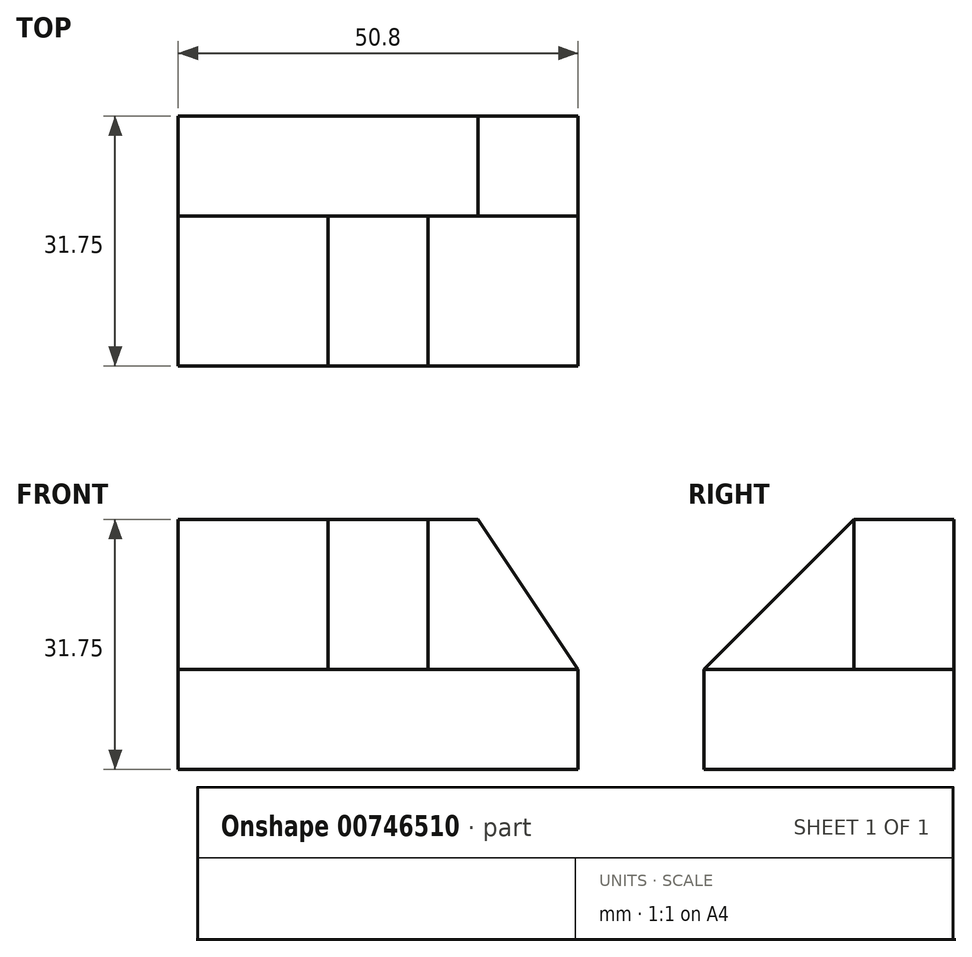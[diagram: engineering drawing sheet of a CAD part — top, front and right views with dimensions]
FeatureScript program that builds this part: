
annotation { "Feature Type Name" : "Feature", "Feature Type Description" : "" }
export const myFeature = defineFeature(function(context is Context, id is Id, definition is map)
    precondition{}
    {
        {
            var Q0;
            Q0=qCreatedBy(makeId("Front.planeOp"),FACE);
            var sketch = newSketch(context, id + "F0", { "sketchPlane" : qUnion([Q0])});
            skLineSegment(sketch, "E0", {"start": v(0, 0) * mm, "end": v(50.8, 0) * mm});
            skLineSegment(sketch, "E1", {"start": v(50.8, 0) * mm, "end": v(50.8, 31.75) * mm});
            skLineSegment(sketch, "E2", {"start": v(50.8, 31.75) * mm, "end": v(0, 31.75) * mm});
            skLineSegment(sketch, "E3", {"start": v(0, 31.75) * mm, "end": v(0, 0) * mm});
            skSolve(sketch);
        }
        {
            var Q0;
            Q0 = qSketchRegion(id + "F0", true);
            extrude(context, id + "F1", {"entities" : qUnion([Q0]), "depth" : 31.75 * mm, "offsetDistance" : 25.4 * mm});
        }
        {
            var Q0;
            Q0=makeQuery(id+"F1.opExtrude","CAP_FACE",FACE,{"disambiguationData":[OSD([sQuery(id+"F0.wireOp",EDGE,"E0"),sQuery(id+"F0.wireOp",EDGE,"E1"),sQuery(id+"F0.wireOp",EDGE,"E2"),sQuery(id+"F0.wireOp",EDGE,"E3")])],"isStart":false});
            var sketch = newSketch(context, id + "F2", { "sketchPlane" : qUnion([Q0])});
            skLineSegment(sketch, "E4", {"start": v(25.4, 31.75) * mm, "end": v(25.4, 25.4) * mm});
            skLineSegment(sketch, "E5", {"start": v(25.4, 25.4) * mm, "end": v(31.75, 25.4) * mm});
            skLineSegment(sketch, "E6", {"start": v(31.75, 25.4) * mm, "end": v(31.75, 31.75) * mm});
            skLineSegment(sketch, "E7", {"start": v(31.75, 31.75) * mm, "end": v(25.4, 31.75) * mm});
            skSolve(sketch);
        }
        {
            var Q0;
            Q0=makeQuery(id+"F1.opExtrude","SWEPT_FACE",FACE,{"disambiguationData":[OSD([sQuery(id+"F0.wireOp",EDGE,"E1")])]});
            var sketch = newSketch(context, id + "F3", { "sketchPlane" : qUnion([Q0])});
            skLineSegment(sketch, "E8", {"start": v(-31.75, 12.7) * mm, "end": v(-12.7, 12.7) * mm});
            skLineSegment(sketch, "E9", {"start": v(-12.7, 12.7) * mm, "end": v(-12.7, 31.75) * mm});
            skLineSegment(sketch, "E10", {"start": v(-12.7, 31.75) * mm, "end": v(-31.75, 31.75) * mm});
            skLineSegment(sketch, "E11", {"start": v(-31.75, 31.75) * mm, "end": v(-31.75, 12.7) * mm});
            skSolve(sketch);
        }
        {
            var Q0;
            Q0=makeQuery(id+"F3.imprint","IMPRINT",FACE,{"disambiguationData":[TD([[makeQuery(id+"F3.imprint","IMPRINT",EDGE,{"derivedFrom":sQuery(id+"F3.wireOp",EDGE,"E8")}),1.0]])]});
            extrude(context, id + "F4", {"entities" : qUnion([Q0]), "operationType" : NewBodyOperationType.REMOVE, "oppositeDirection" : true, "depth" : 19.05 * mm, "offsetDistance" : 25.4 * mm});
        }
        {
            var Q0;
            Q0=makeQuery(id+"F1.opExtrude","SWEPT_FACE",FACE,{"disambiguationData":[OSD([sQuery(id+"F0.wireOp",EDGE,"E3")])]});
            var sketch = newSketch(context, id + "F5", { "sketchPlane" : qUnion([Q0])});
            skLineSegment(sketch, "E12", {"start": v(31.75, 12.7) * mm, "end": v(12.7, 12.7) * mm});
            skLineSegment(sketch, "E13", {"start": v(12.7, 12.7) * mm, "end": v(12.7, 31.75) * mm});
            skLineSegment(sketch, "E14", {"start": v(12.7, 31.75) * mm, "end": v(31.75, 31.75) * mm});
            skLineSegment(sketch, "E15", {"start": v(31.75, 31.75) * mm, "end": v(31.75, 12.7) * mm});
            skSolve(sketch);
        }
        {
            var Q0;
            Q0=makeQuery(id+"F5.imprint","IMPRINT",FACE,{"disambiguationData":[TD([[makeQuery(id+"F5.imprint","IMPRINT",EDGE,{"derivedFrom":sQuery(id+"F5.wireOp",EDGE,"E12")}),-1.0]])]});
            extrude(context, id + "F6", {"entities" : qUnion([Q0]), "operationType" : NewBodyOperationType.REMOVE, "oppositeDirection" : true, "depth" : 19.05 * mm, "offsetDistance" : 25.4 * mm});
        }
        {
            var Q0;
            Q0=makeQuery(id+"F4.boolean.opBoolean","COPY",FACE,{"derivedFrom":makeQuery(id+"F4.opExtrude","CAP_FACE",FACE,{"disambiguationData":[OSD([sQuery(id+"F3.wireOp",EDGE,"E8"),sQuery(id+"F3.wireOp",EDGE,"E9"),sQuery(id+"F3.wireOp",EDGE,"E10"),sQuery(id+"F3.wireOp",EDGE,"E11")])],"isStart":false})});
            var sketch = newSketch(context, id + "F7", { "sketchPlane" : qUnion([Q0])});
            skLineSegment(sketch, "E16", {"start": v(-12.7, 31.75) * mm, "end": v(-31.75, 12.7) * mm});
            skLineSegment(sketch, "E17", {"start": v(-31.75, 12.7) * mm, "end": v(-31.75, 31.75) * mm});
            skLineSegment(sketch, "E18", {"start": v(-31.75, 31.75) * mm, "end": v(-12.7, 31.75) * mm});
            skSolve(sketch);
        }
        {
            var Q0;
            Q0=makeQuery(id+"F7.imprint","IMPRINT",FACE,{"disambiguationData":[TD([[makeQuery(id+"F7.imprint","IMPRINT",EDGE,{"derivedFrom":sQuery(id+"F7.wireOp",EDGE,"E16")}),-1.0]])]});
            extrude(context, id + "F8", {"entities" : qUnion([Q0]), "operationType" : NewBodyOperationType.REMOVE, "oppositeDirection" : true, "depth" : 25.4 * mm, "offsetDistance" : 25.4 * mm});
        }
        {
            var Q0;
            Q0=makeQuery(id+"F4.boolean.opBoolean","COPY",FACE,{"derivedFrom":makeQuery(id+"F4.opExtrude","SWEPT_FACE",FACE,{"disambiguationData":[OSD([sQuery(id+"F3.wireOp",EDGE,"E9")])]})});
            var sketch = newSketch(context, id + "F9", { "sketchPlane" : qUnion([Q0])});
            skLineSegment(sketch, "E19", {"start": v(38.1, 31.75) * mm, "end": v(38.1, 25.4) * mm});
            skLineSegment(sketch, "E20", {"start": v(38.1, 25.4) * mm, "end": v(31.75, 25.4) * mm});
            skLineSegment(sketch, "E21", {"start": v(31.75, 25.4) * mm, "end": v(31.75, 31.75) * mm});
            skLineSegment(sketch, "E22", {"start": v(31.75, 31.75) * mm, "end": v(38.1, 31.75) * mm});
            skLineSegment(sketch, "E23", {"start": v(38.1, 31.75) * mm, "end": v(50.8, 12.7) * mm});
            skLineSegment(sketch, "E24", {"start": v(50.8, 12.7) * mm, "end": v(50.8, 31.75) * mm});
            skLineSegment(sketch, "E25", {"start": v(50.8, 31.75) * mm, "end": v(38.1, 31.75) * mm});
            skSolve(sketch);
        }
        {
            var Q0;
            Q0=makeQuery(id+"F9.imprint","IMPRINT",FACE,{"disambiguationData":[TD([[makeQuery(id+"F9.imprint","IMPRINT",EDGE,{"derivedFrom":sQuery(id+"F9.wireOp",EDGE,"E23")}),1.0]])]});
            extrude(context, id + "F10", {"entities" : qUnion([Q0]), "operationType" : NewBodyOperationType.REMOVE, "oppositeDirection" : true, "depth" : 38.1 * mm, "offsetDistance" : 25.4 * mm});
        }
    });
